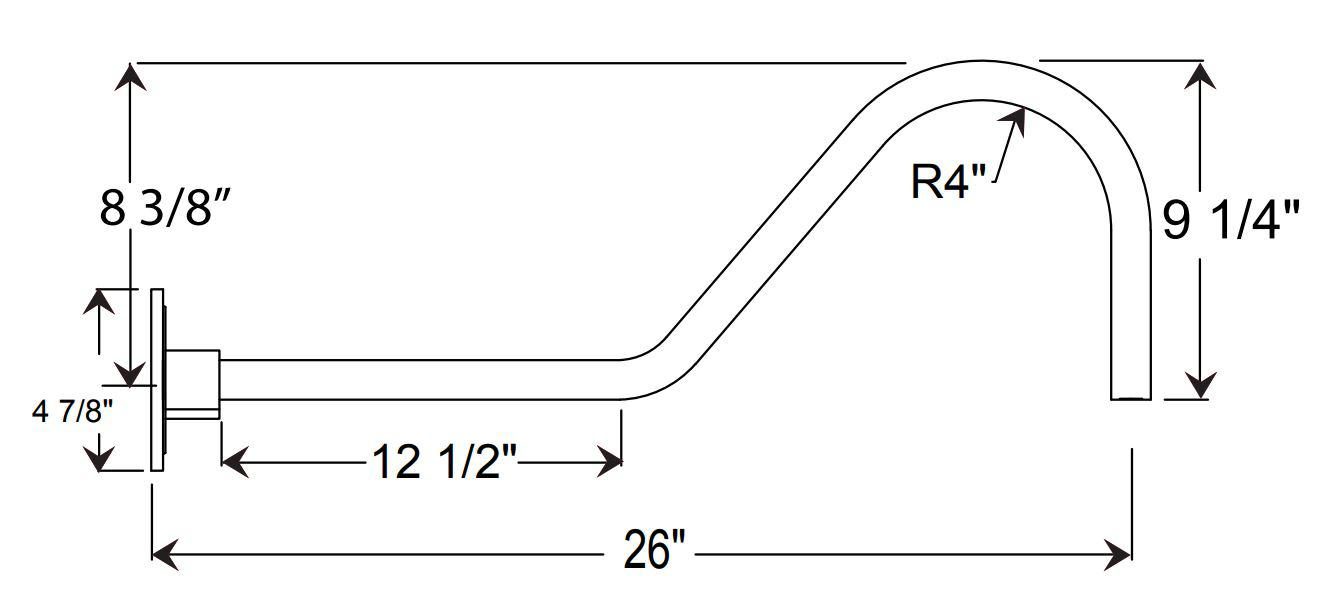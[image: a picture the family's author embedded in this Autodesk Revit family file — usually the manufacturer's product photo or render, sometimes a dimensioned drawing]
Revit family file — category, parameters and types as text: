
# Revit family: Sycamore 12,16,20,24 LED
name_source: partatom
category: Lighting Fixtures
units: mm (PartAtom-declared; Revit-internal decimal feet)

## family parameters
Always vertical = Yes
Cut with Voids When Loaded = No
Light Source = Yes
OmniClass Number = 23.80.70.00
OmniClass Title = Lighting
Part Type = Normal
Room Calculation Point = No
Round Connector Dimension = Use Diameter
Shared = No
Work Plane-Based = No

## types (4) — shared parameters
Body Colour = Spun aluminium
Body Material = body
CRI = >90
Color Filter = 16777215
Construction Material = Heavy Duty spun aluminum.
Default Elevation = 0' - 0"
Description = 120-277 Voltage
Dimming = 1%
Dimming Lamp Color Temperature Shift = <None>
Efficiency = 65-125 lumens per watt
Fixture Finish = Fixture finish
GLASS = Glass
Lamp = LED
Life = L70 50,000 hours
Load Classification = Lighting
Manufacturer = ANP Lighting
Power Factor = 1
Tilt Angle = 90.00°
URL = https://www.anplighting.com
Voltage = 277 V
Warranty = 5 year limited warranty

## per-type parameters (varying)
| type | Apparent Load | Fixture Diameter | Fixture Height | MDS12 | MDS16 | MDS20 | MDS24 | Photometric Web File | Wattage Comments | Weight |
| MDS12 | 10 VA | 1' - 0" | 0' - 7 1/2" | Yes | No | No | No | MDS12M010LD35K.IES | 10W | 4.5 lbs |
| MDS16 | 16 VA | 1' - 4" | 0' - 10" | No | Yes | No | No | MDS12M010LD35K.IES | 16W | 5.0 lbs |
| MDS20 | 16 VA | 1' - 8" | 1' - 0 1/2" | No | No | Yes | No | MDS20M016LD35K.IES | 16W | 5.5 lbs |
| MDS24 | 24 VA | 1' - 8" | 1' - 3" | No | No | No | Yes | MDS20M016LD35K.IES | 24W | 6.0 lbs |

note: column(s) folded — value = type name in every type: Model

## geometry (parser evidence)
native form markers: Sweep x31
no freeform markers — native parametric forms only
